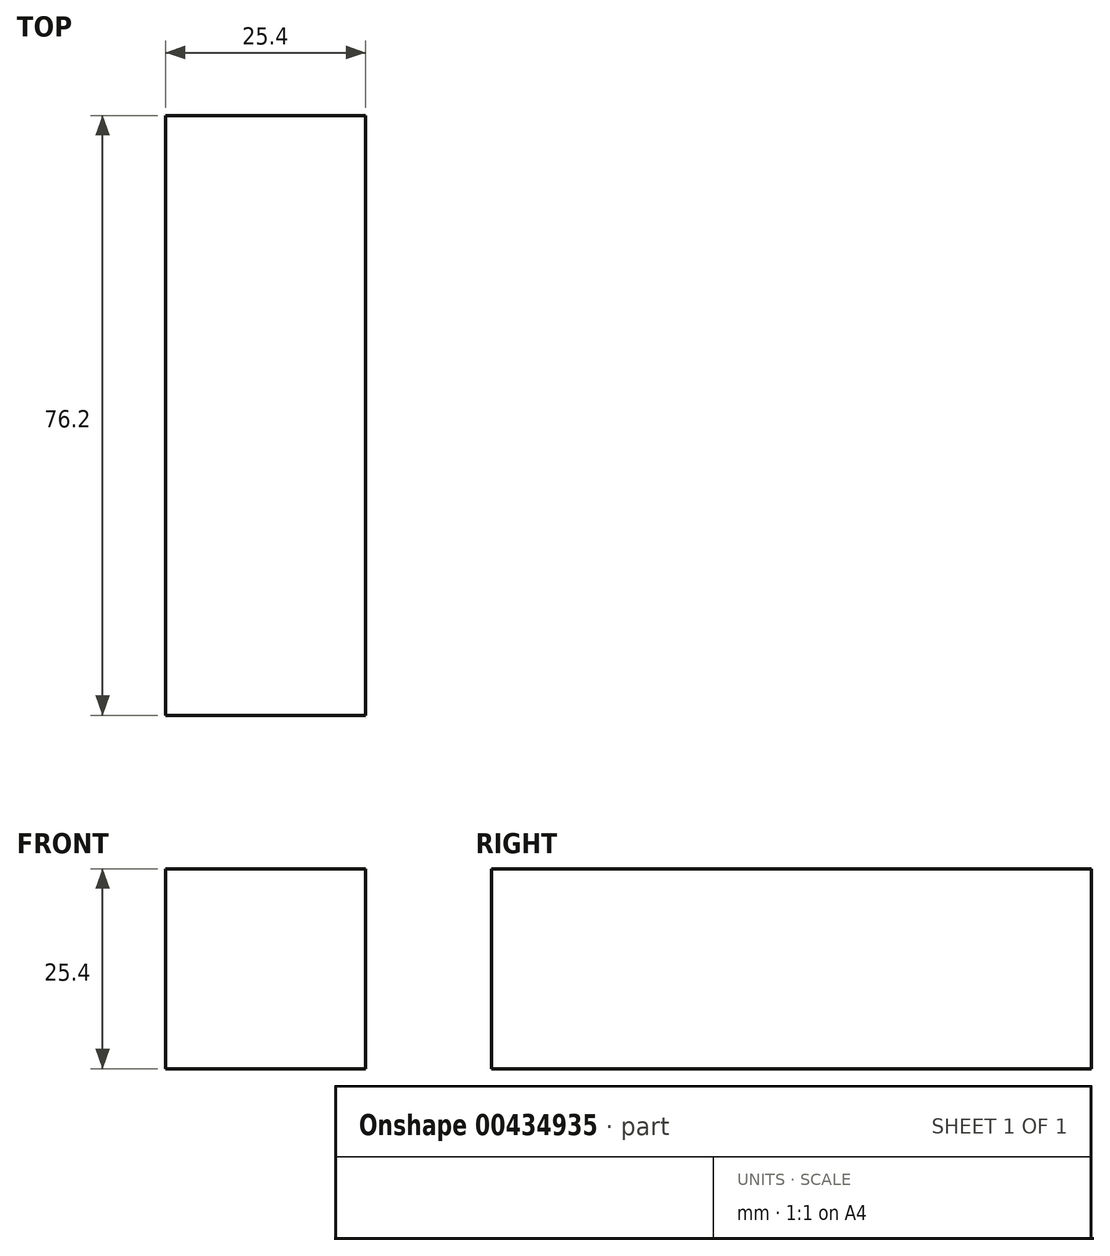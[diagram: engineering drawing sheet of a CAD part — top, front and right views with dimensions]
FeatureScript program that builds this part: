
annotation { "Feature Type Name" : "Feature", "Feature Type Description" : "" }
export const myFeature = defineFeature(function(context is Context, id is Id, definition is map)
    precondition{}
    {
        {
            var Q0;
            Q0=qCreatedBy(makeId("Front.planeOp"),FACE);
            var sketch = newSketch(context, id + "F0", { "sketchPlane" : qUnion([Q0])});
            skLineSegment(sketch, "E0.bottom", {"start": v(-5.96, -5.86) * mm, "end": v(19.44, -5.86) * mm});
            skLineSegment(sketch, "E0.top", {"start": v(-5.96, 19.54) * mm, "end": v(19.44, 19.54) * mm});
            skLineSegment(sketch, "E0.left", {"start": v(-5.96, -5.86) * mm, "end": v(-5.96, 19.54) * mm});
            skLineSegment(sketch, "E0.right", {"start": v(19.44, -5.86) * mm, "end": v(19.44, 19.54) * mm});
            skSolve(sketch);
        }
        {
            var Q0;
            Q0=makeQuery(id+"F0.imprint","IMPRINT",FACE,{"disambiguationData":[TD([[makeQuery(id+"F0.imprint","IMPRINT",EDGE,{"derivedFrom":sQuery(id+"F0.wireOp",EDGE,"E0.bottom")}),1.0]])]});
            extrude(context, id + "F1", {"entities" : qUnion([Q0]), "depth" : 76.2 * mm});
        }
    });
